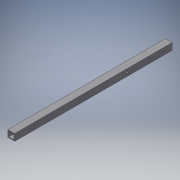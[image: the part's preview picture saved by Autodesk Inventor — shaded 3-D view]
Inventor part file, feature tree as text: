
AUTODESK INVENTOR PART (.ipt)
format: ipt  version: 2018 (Build 220112000, 112)  size: 141,824 bytes
history: native  units: in
note: dims shown in document units (in); Inventor stores cm internally (conversion verified against a paired STEP export)
features: extrude x3, sketch x3
ambient origin geometry x8: Origin, YZ Plane, XZ Plane, XY Plane, X Axis, Y Axis, Z Axis, Center Point
bodies: Solid1 (feature_tree)
feature tree (6):
  extrude  "Extrusion1"  Depth=1.0in
  extrude  "Extrusion2"  Depth=23.0in TaperAngle=0.0deg
  extrude  "Extrusion3"  Depth=1.0in
  sketch  "Sketch1"  dims[d0=1.0in d1=1.0in]
  sketch  "Sketch2"  dims[d2=0.125in d3=23.0in d4=0.0in]
  sketch  "Sketch3"  dims[d5=0.5in d6=1.0in d7=0.5in d8=1.0in d9=0.2031in d10=23.0in d11=0.0in d12=7.5in d13=0.2031in d14=1.0in d15=2.0in d16=23.0in d17=0.0in d18=0.2031in d19=0.2031in d20=0.2031in]
